# Revit family: PRD_FrankeWS_SpDshs_CHRONOSSoapAndShowerGelTray_CHRX644
name_source: partatom
category: Specialty Equipment
revit_build: Autodesk Revit 2018 (Build: 20190510_1515(x64)
units: mm (PartAtom-declared; Revit-internal decimal feet)

## family parameters
Cut with Voids When Loaded = No
Host = Face
OmniClass Number = 23.45.05.14.99
OmniClass Title = Other Sanitary Washing Plumbing Fixtures
Part Type = Normal
Room Calculation Point = No
Round Connector Dimension = Use Diameter
Shared = No

## types (1)
- CHRX644
    AssetType = Fixed
    BIMObjectName = PRD_AR_SoapDishes_CHRONOSSoapAndShowerGelTray_CHRX644
    Category = Pr_40_20_76_82, Soap dishes
    Default Elevation = 1000 mm  [stored 3.28084 ft]
    Description = Soap and shower gel holder for wall mounting, nickel chromium steel, surface satin finish, material thickness 2.0 mm, deep drawn soap tray with drain holes, lateral shelf, rounded edges, includes stainless steel screws and dowels.
    DurationUnit = year
    Features = nickel chromium steel, surface satin finish, material thickness 2.0 mm
    Finish = satin finish
    GrossWeight = 0.47 kg
    IfcExportAs = IfcSanitaryTerminalType
    IfcExportType = USERDEFINED
    IntegralAccessories = includes stainless steel screws and dowels
    MainColor = stainless steel
    MainMaterial = PRD_AR_Steel_NickelChromium_SatinFinished
    Manufacturer = KWC Group AG
    ManufacturerName = KWC Group AG
    ManufacturerURL = www.kwc.com
    Material = Stainless steel
    MaterialCode = 1.4301 Chrome Nickel steel V2A
    MaterialThickness = 2.00 mm
    Model = CHRX644
    ModelNumber = 2000100804
    ModelReference = CHRX644
    NBSDescription = Soap dishes
    NBSReference = 45-35-72/356
    Name = CHRONOS Soap and shower gel tray CHRX644
    NetWeight = 0.41 kg
    NominalDepth = 100 mm  [stored 0.328084 ft]
    NominalHeight = 40 mm  [stored 0.131234 ft]
    NominalLength = 0 mm  [stored 0 ft]
    NominalWidth = 180 mm  [stored 0.590551 ft]
    ProductCode = 201.0601.403
    ProductInformation = https://pim.kwc.com
    Size = 180 x 40 x 100 mm (W x H x D)
    Status = New
    TypeOfFixing = Screw
    TypeOfMounting = Wall mounting
    URL = www.kwc.com
    Uniclass2015Code = Pr_40_20_76_82
    Uniclass2015Title = Soap dishes
    Uniclass2015Version = Products v1.23
    Version = 1
    WarrantyDurationUnit = year

note: [stored X ft] marks values corroborated as IEEE doubles in the binary element streams (Revit-internal decimal feet)

## geometry (parser evidence)
native form markers: Sweep x2
no freeform markers — native parametric forms only
